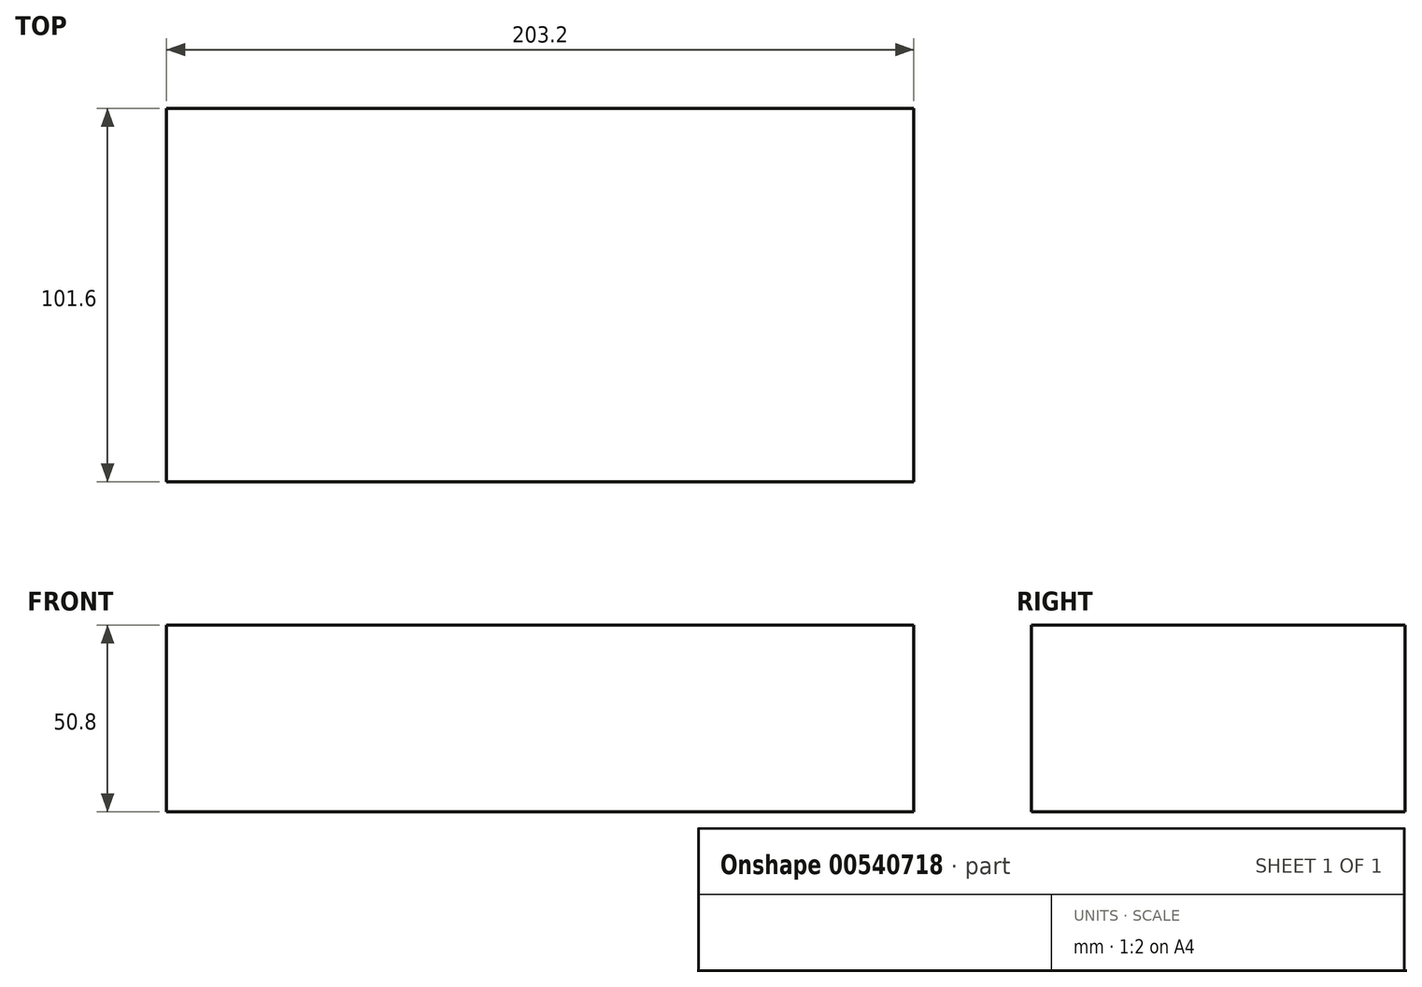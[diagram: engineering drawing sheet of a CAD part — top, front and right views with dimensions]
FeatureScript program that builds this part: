
annotation { "Feature Type Name" : "Feature", "Feature Type Description" : "" }
export const myFeature = defineFeature(function(context is Context, id is Id, definition is map)
    precondition{}
    {
        {
            var Q0;
            Q0=qCreatedBy(makeId("Front.planeOp"),FACE);
            var sketch = newSketch(context, id + "F0", { "sketchPlane" : qUnion([Q0])});
            skLineSegment(sketch, "E0.bottom", {"start": v(0, 0) * mm, "end": v(203.2, 0) * mm});
            skLineSegment(sketch, "E0.top", {"start": v(0, 50.8) * mm, "end": v(203.2, 50.8) * mm});
            skLineSegment(sketch, "E0.left", {"start": v(0, 0) * mm, "end": v(0, 50.8) * mm});
            skLineSegment(sketch, "E0.right", {"start": v(203.2, 0) * mm, "end": v(203.2, 50.8) * mm});
            skSolve(sketch);
        }
        {
            var Q0;
            Q0 = qConstructionFilter(qBodyType(qCreatedBy(id + "F0" ,EDGE), BodyType.WIRE), ConstructionObject.NO);
            extrude(context, id + "F1", {"bodyType" : ToolBodyType.SURFACE, "surfaceEntities" : qUnion([Q0]), "depth" : 101.6 * mm, "offsetDistance" : 25.4 * mm});
        }
    });
